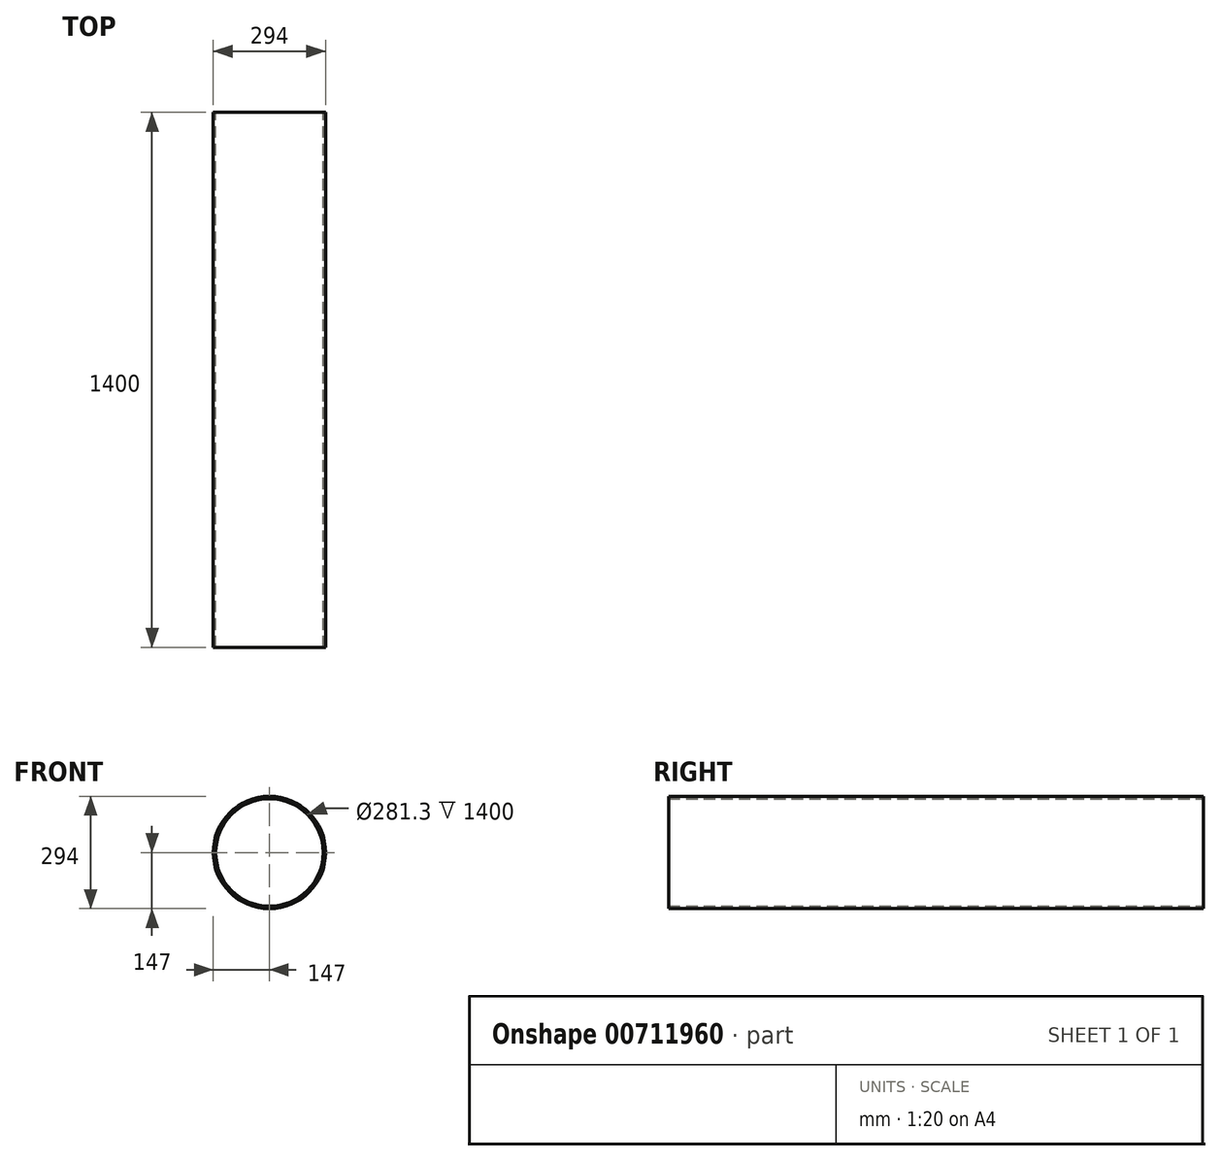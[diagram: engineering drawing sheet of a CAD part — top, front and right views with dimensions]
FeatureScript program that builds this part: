
annotation { "Feature Type Name" : "Feature", "Feature Type Description" : "" }
export const myFeature = defineFeature(function(context is Context, id is Id, definition is map)
    precondition{}
    {
        {
            var Q0;
            Q0=qCreatedBy(makeId("Front.planeOp"),FACE);
            var sketch = newSketch(context, id + "F0", { "sketchPlane" : qUnion([Q0])});
            skCircle(sketch, "E0", {"center": v(0, 0) * mm, "radius": 147 * mm});
            skCircle(sketch, "E1", {"center": v(0, 0) * mm, "radius": 140.65 * mm});
            skSolve(sketch);
        }
        {
            var Q0;
            Q0 = qSketchRegion(id + "F0", true);
            extrude(context, id + "F1", {"entities" : qUnion([Q0]), "endBound" : BoundingType.SYMMETRIC, "depth" : 1400 * mm, "offsetDistance" : 25 * mm});
        }
    });
